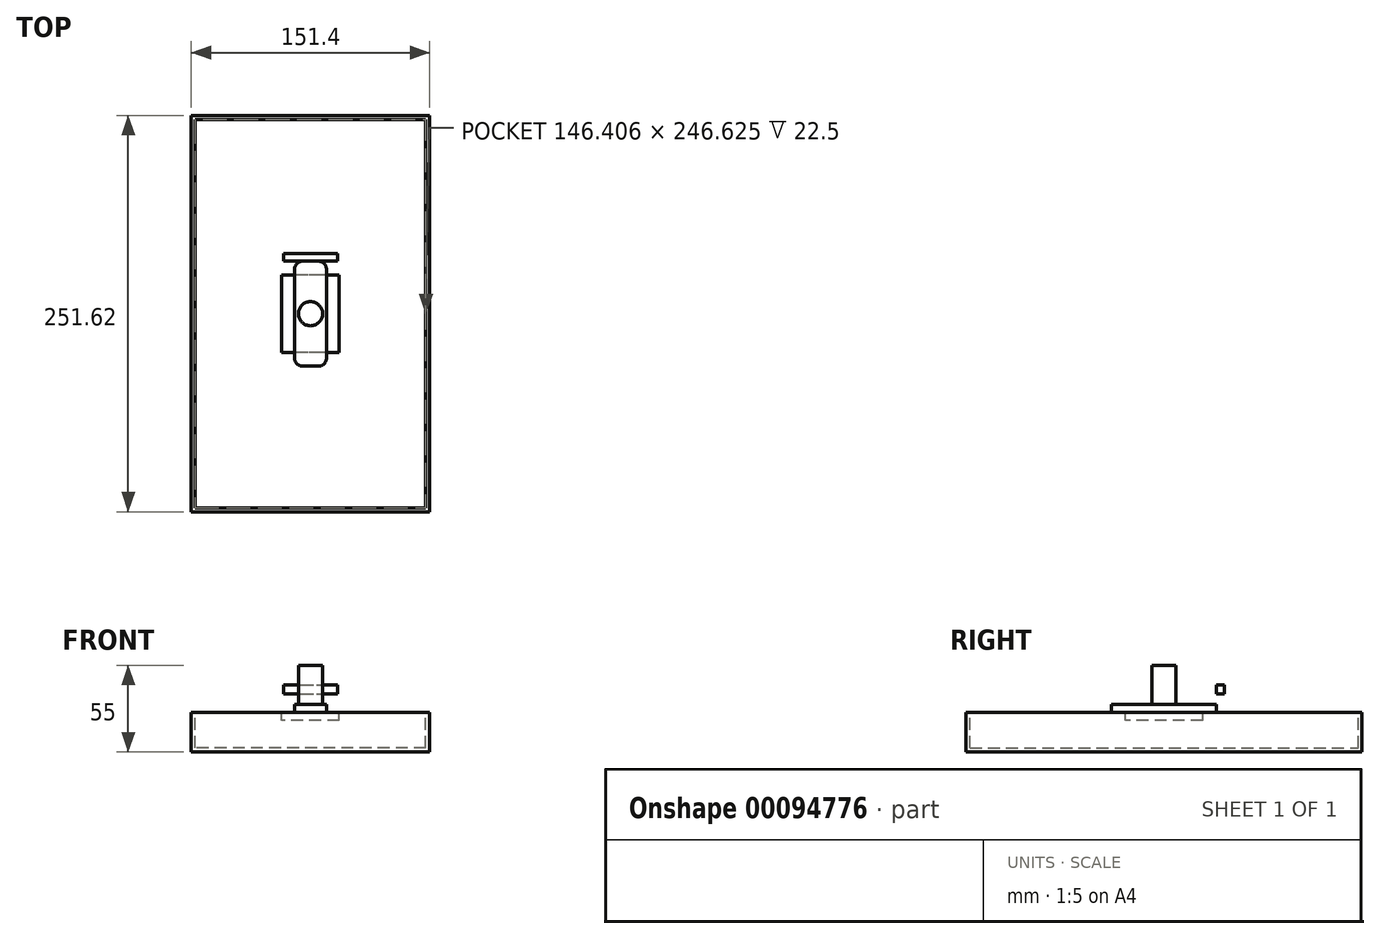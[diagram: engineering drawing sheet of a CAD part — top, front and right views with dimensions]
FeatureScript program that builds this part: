
annotation { "Feature Type Name" : "Feature", "Feature Type Description" : "" }
export const myFeature = defineFeature(function(context is Context, id is Id, definition is map)
    precondition{}
    {
        {
            var Q0;
            Q0=qCreatedBy(makeId("Top.planeOp"),FACE);
            var sketch = newSketch(context, id + "F0", { "sketchPlane" : qUnion([Q0])});
            skLineSegment(sketch, "E0.bottom", {"start": v(18.23, 24.57) * mm, "end": v(-18.23, 24.57) * mm});
            skLineSegment(sketch, "E0.top", {"start": v(18.23, -24.57) * mm, "end": v(-18.23, -24.57) * mm});
            skLineSegment(sketch, "E0.left", {"start": v(18.23, 24.57) * mm, "end": v(18.23, -24.57) * mm});
            skLineSegment(sketch, "E0.right", {"start": v(-18.23, 24.57) * mm, "end": v(-18.23, -24.57) * mm});
            skPoint(sketch, "E0.middle", {"position": v(0, 0) * mm});
            skSolve(sketch);
        }
        {
            var Q0;
            Q0 = qSketchRegion(id + "F0", true);
            extrude(context, id + "F1", {"entities" : qUnion([Q0]), "oppositeDirection" : true, "depth" : 5 * mm});
        }
        {
            var Q0;
            Q0=makeQuery(id+"F1.opExtrude","CAP_FACE",FACE,{"disambiguationData":[OSD([sQuery(id+"F0.wireOp",EDGE,"E0.bottom"),sQuery(id+"F0.wireOp",EDGE,"E0.top"),sQuery(id+"F0.wireOp",EDGE,"E0.left"),sQuery(id+"F0.wireOp",EDGE,"E0.right")])],"isStart":true});
            var sketch = newSketch(context, id + "F2", { "sketchPlane" : qUnion([Q0])});
            skLineSegment(sketch, "E1.bottom", {"start": v(10.1, 33.33) * mm, "end": v(-10.1, 33.33) * mm});
            skLineSegment(sketch, "E1.top", {"start": v(10.1, -33.33) * mm, "end": v(-10.1, -33.33) * mm});
            skLineSegment(sketch, "E1.left", {"start": v(10.1, 33.33) * mm, "end": v(10.1, -33.33) * mm});
            skLineSegment(sketch, "E1.right", {"start": v(-10.1, 33.33) * mm, "end": v(-10.1, -33.33) * mm});
            skPoint(sketch, "E1.middle", {"position": v(0, 0) * mm});
            skSolve(sketch);
        }
        {
            var Q0;
            Q0 = qSketchRegion(id + "F2", true);
            extrude(context, id + "F3", {"entities" : qUnion([Q0]), "depth" : 5 * mm});
        }
        {
            var Q0;
            Q0=makeQuery(id+"F3.opExtrude","SWEPT_EDGE",EDGE,{"disambiguationData":[OSD([sQuery(id+"F2.wireOp",EDGE,"E1.top"),sQuery(id+"F2.wireOp",EDGE,"E1.right")])]});
            var Q1;
            Q1=makeQuery(id+"F3.opExtrude","SWEPT_EDGE",EDGE,{"disambiguationData":[OSD([sQuery(id+"F2.wireOp",EDGE,"E1.top"),sQuery(id+"F2.wireOp",EDGE,"E1.left")])]});
            var Q2;
            Q2=makeQuery(id+"F3.opExtrude","SWEPT_EDGE",EDGE,{"disambiguationData":[OSD([sQuery(id+"F2.wireOp",EDGE,"E1.bottom"),sQuery(id+"F2.wireOp",EDGE,"E1.left")])]});
            var Q3;
            Q3=makeQuery(id+"F3.opExtrude","SWEPT_EDGE",EDGE,{"disambiguationData":[OSD([sQuery(id+"F2.wireOp",EDGE,"E1.bottom"),sQuery(id+"F2.wireOp",EDGE,"E1.right")])]});
            fillet(context, id + "F4", {"entities" : qUnion([Q0, Q1, Q2, Q3]), "radius" : 5 * mm, "tangentPropagation" : true, "allowEdgeOverflow" : false});
        }
        {
            var Q0;
            Q0=makeQuery(id+"F3.opExtrude","CAP_FACE",FACE,{"disambiguationData":[OSD([sQuery(id+"F2.wireOp",EDGE,"E1.bottom"),sQuery(id+"F2.wireOp",EDGE,"E1.top"),sQuery(id+"F2.wireOp",EDGE,"E1.left"),sQuery(id+"F2.wireOp",EDGE,"E1.right")])],"isStart":false});
            var sketch = newSketch(context, id + "F5", { "sketchPlane" : qUnion([Q0])});
            skCircle(sketch, "E2", {"center": v(0, 0) * mm, "radius": 7.68 * mm});
            skSolve(sketch);
        }
        {
            var Q0;
            Q0 = qSketchRegion(id + "F5", true);
            extrude(context, id + "F6", {"entities" : qUnion([Q0]), "operationType" : NewBodyOperationType.ADD, "depth" : 25 * mm});
        }
        {
            var Q0;
            Q0=makeQuery(id+"F3.opExtrude","SWEPT_FACE",FACE,{"disambiguationData":[OSD([sQuery(id+"F2.wireOp",EDGE,"E1.bottom")])]});
            var sketch = newSketch(context, id + "F7", { "sketchPlane" : qUnion([Q0])});
            skLineSegment(sketch, "E3.bottom", {"start": v(17.06, 17.39) * mm, "end": v(-17.06, 17.39) * mm});
            skLineSegment(sketch, "E3.top", {"start": v(17.06, 11.8) * mm, "end": v(-17.06, 11.8) * mm});
            skLineSegment(sketch, "E3.left", {"start": v(17.06, 17.39) * mm, "end": v(17.06, 11.8) * mm});
            skLineSegment(sketch, "E3.right", {"start": v(-17.06, 17.39) * mm, "end": v(-17.06, 11.8) * mm});
            skPoint(sketch, "E3.middle", {"position": v(0, 14.6) * mm});
            skSolve(sketch);
        }
        {
            var Q0;
            Q0 = qSketchRegion(id + "F7", true);
            extrude(context, id + "F8", {"entities" : qUnion([Q0]), "depth" : 5 * mm});
        }
        {
            var Q0;
            Q0=qCreatedBy(makeId("Top.planeOp"),FACE);
            var sketch = newSketch(context, id + "F9", { "sketchPlane" : qUnion([Q0])});
            skLineSegment(sketch, "E4.bottom", {"start": v(75.7, -125.81) * mm, "end": v(-75.7, -125.81) * mm});
            skLineSegment(sketch, "E4.top", {"start": v(75.7, 125.81) * mm, "end": v(-75.7, 125.81) * mm});
            skLineSegment(sketch, "E4.left", {"start": v(75.7, -125.81) * mm, "end": v(75.7, 125.81) * mm});
            skLineSegment(sketch, "E4.right", {"start": v(-75.7, -125.81) * mm, "end": v(-75.7, 125.81) * mm});
            skPoint(sketch, "E4.middle", {"position": v(0, 0) * mm});
            skSolve(sketch);
        }
        {
            var Q0;
            Q0 = qSketchRegion(id + "F9", true);
            extrude(context, id + "F10", {"entities" : qUnion([Q0]), "oppositeDirection" : true, "depth" : 25 * mm});
        }
        {
            var Q0;
            Q0=makeQuery(id+"F10.opExtrude","CAP_FACE",FACE,{"disambiguationData":[OSD([sQuery(id+"F9.wireOp",EDGE,"E4.bottom"),sQuery(id+"F9.wireOp",EDGE,"E4.top"),sQuery(id+"F9.wireOp",EDGE,"E4.left"),sQuery(id+"F9.wireOp",EDGE,"E4.right")])],"isStart":true});
            shell(context, id + "F11", {"entities" : qUnion([Q0]), "thickness" : 2.5 * mm});
        }
    });
